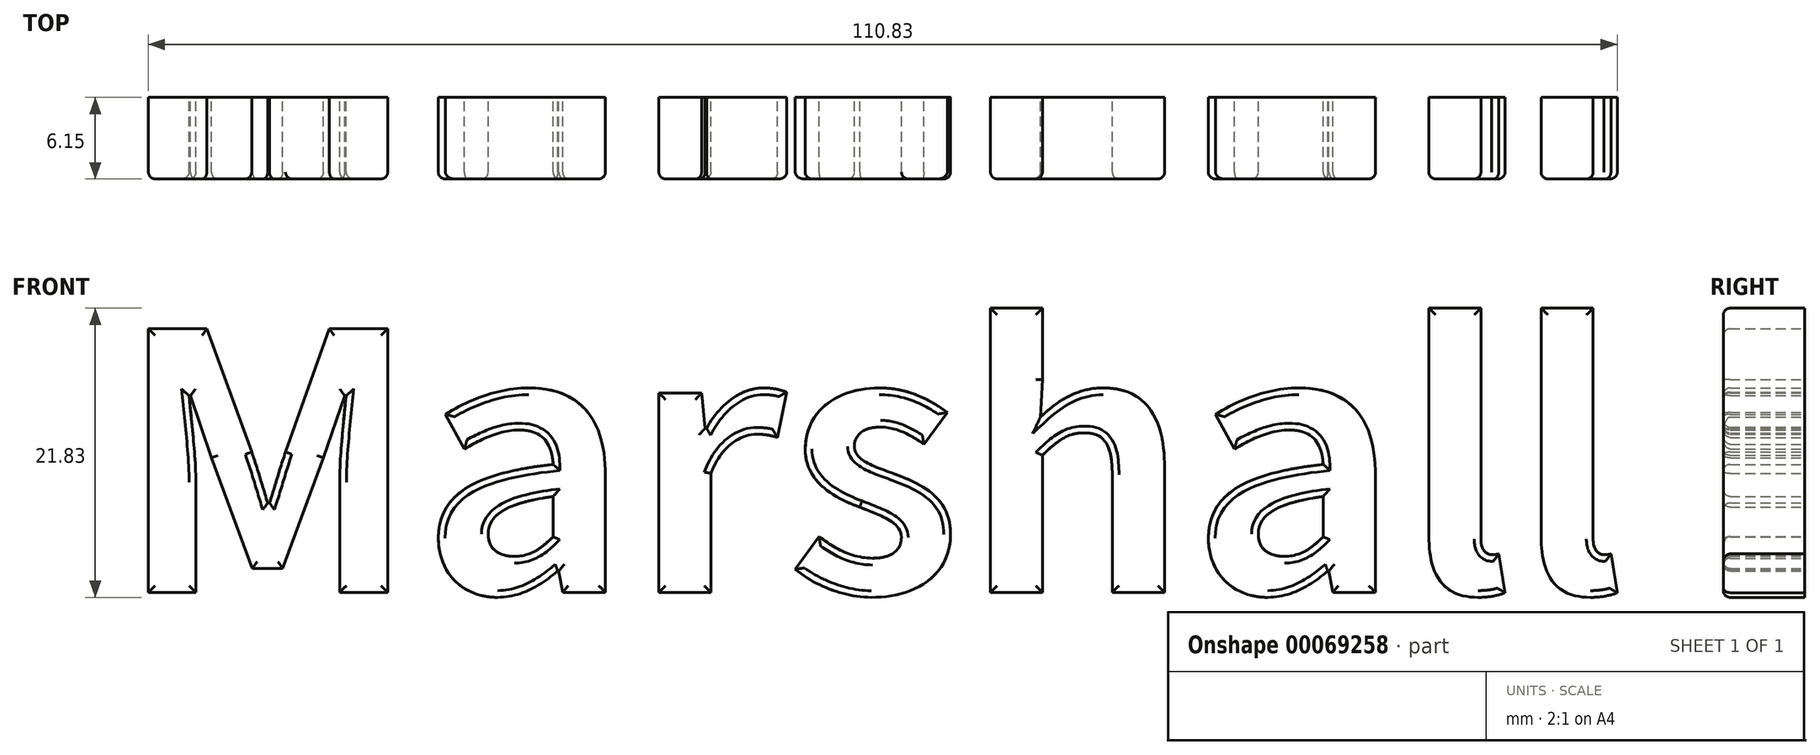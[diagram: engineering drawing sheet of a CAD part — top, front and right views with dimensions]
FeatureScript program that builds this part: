
annotation { "Feature Type Name" : "Feature", "Feature Type Description" : "" }
export const myFeature = defineFeature(function(context is Context, id is Id, definition is map)
    precondition{}
    {
        {
            var Q0;
            Q0=qCreatedBy(makeId("Front.planeOp"),FACE);
            var sketch = newSketch(context, id + "F0", { "sketchPlane" : qUnion([Q0])});
            skText(sketch, "E0", { "text": "Marshall", "fontName": "NotoSansCJKjp-Bold.otf"});
            const initialGuessF0  = {"E0": [-0.07328, 0.02694, 1, 0, 0.01935]};
            skSetInitialGuess(sketch, initialGuessF0);
            skSolve(sketch);
        }
        {
            var Q0;
            Q0 = qSketchRegion(id + "F0", true);
            extrude(context, id + "F1", {"entities" : qUnion([Q0]), "depth" : 6.15 * mm});
        }
        {
            var Q0;
            Q0=makeQuery(id+"F1.opExtrude","CAP_FACE",FACE,{"disambiguationData":[OSD([sQuery(id+"F0.wireOp",EDGE,"E0.sketch_text.stroke-0"),sQuery(id+"F0.wireOp",EDGE,"E0.sketch_text.stroke-1"),sQuery(id+"F0.wireOp",EDGE,"E0.sketch_text.stroke-2"),sQuery(id+"F0.wireOp",EDGE,"E0.sketch_text.stroke-3"),sQuery(id+"F0.wireOp",EDGE,"E0.sketch_text.stroke-4"),sQuery(id+"F0.wireOp",EDGE,"E0.sketch_text.stroke-5"),sQuery(id+"F0.wireOp",EDGE,"E0.sketch_text.stroke-6"),sQuery(id+"F0.wireOp",EDGE,"E0.sketch_text.stroke-7"),sQuery(id+"F0.wireOp",EDGE,"E0.sketch_text.stroke-8"),sQuery(id+"F0.wireOp",EDGE,"E0.sketch_text.stroke-9"),sQuery(id+"F0.wireOp",EDGE,"E0.sketch_text.stroke-10"),sQuery(id+"F0.wireOp",EDGE,"E0.sketch_text.stroke-11"),sQuery(id+"F0.wireOp",EDGE,"E0.sketch_text.stroke-12"),sQuery(id+"F0.wireOp",EDGE,"E0.sketch_text.stroke-13"),sQuery(id+"F0.wireOp",EDGE,"E0.sketch_text.stroke-14"),sQuery(id+"F0.wireOp",EDGE,"E0.sketch_text.stroke-15"),sQuery(id+"F0.wireOp",EDGE,"E0.sketch_text.stroke-16"),sQuery(id+"F0.wireOp",EDGE,"E0.sketch_text.stroke-17"),sQuery(id+"F0.wireOp",EDGE,"E0.sketch_text.stroke-18"),sQuery(id+"F0.wireOp",EDGE,"E0.sketch_text.stroke-19"),sQuery(id+"F0.wireOp",EDGE,"E0.sketch_text.stroke-20"),sQuery(id+"F0.wireOp",EDGE,"E0.sketch_text.stroke-21")])],"isStart":false});
            var Q1;
            Q1=makeQuery(id+"F1.opExtrude","CAP_FACE",FACE,{"disambiguationData":[OSD([sQuery(id+"F0.wireOp",EDGE,"E0.sketch_text.stroke-22"),sQuery(id+"F0.wireOp",EDGE,"E0.sketch_text.stroke-23"),sQuery(id+"F0.wireOp",EDGE,"E0.sketch_text.stroke-24"),sQuery(id+"F0.wireOp",EDGE,"E0.sketch_text.stroke-25"),sQuery(id+"F0.wireOp",EDGE,"E0.sketch_text.stroke-26"),sQuery(id+"F0.wireOp",EDGE,"E0.sketch_text.stroke-27"),sQuery(id+"F0.wireOp",EDGE,"E0.sketch_text.stroke-28"),sQuery(id+"F0.wireOp",EDGE,"E0.sketch_text.stroke-29"),sQuery(id+"F0.wireOp",EDGE,"E0.sketch_text.stroke-30"),sQuery(id+"F0.wireOp",EDGE,"E0.sketch_text.stroke-31"),sQuery(id+"F0.wireOp",EDGE,"E0.sketch_text.stroke-32"),sQuery(id+"F0.wireOp",EDGE,"E0.sketch_text.stroke-33"),sQuery(id+"F0.wireOp",EDGE,"E0.sketch_text.stroke-34"),sQuery(id+"F0.wireOp",EDGE,"E0.sketch_text.stroke-35"),sQuery(id+"F0.wireOp",EDGE,"E0.sketch_text.stroke-36"),sQuery(id+"F0.wireOp",EDGE,"E0.sketch_text.stroke-37")])],"isStart":false});
            var Q2;
            Q2=makeQuery(id+"F1.opExtrude","CAP_FACE",FACE,{"disambiguationData":[OSD([sQuery(id+"F0.wireOp",EDGE,"E0.sketch_text.stroke-38"),sQuery(id+"F0.wireOp",EDGE,"E0.sketch_text.stroke-39"),sQuery(id+"F0.wireOp",EDGE,"E0.sketch_text.stroke-40"),sQuery(id+"F0.wireOp",EDGE,"E0.sketch_text.stroke-41"),sQuery(id+"F0.wireOp",EDGE,"E0.sketch_text.stroke-42"),sQuery(id+"F0.wireOp",EDGE,"E0.sketch_text.stroke-43"),sQuery(id+"F0.wireOp",EDGE,"E0.sketch_text.stroke-44"),sQuery(id+"F0.wireOp",EDGE,"E0.sketch_text.stroke-45"),sQuery(id+"F0.wireOp",EDGE,"E0.sketch_text.stroke-46"),sQuery(id+"F0.wireOp",EDGE,"E0.sketch_text.stroke-47"),sQuery(id+"F0.wireOp",EDGE,"E0.sketch_text.stroke-48")])],"isStart":false});
            var Q3;
            Q3=makeQuery(id+"F1.opExtrude","CAP_FACE",FACE,{"disambiguationData":[OSD([sQuery(id+"F0.wireOp",EDGE,"E0.sketch_text.stroke-49"),sQuery(id+"F0.wireOp",EDGE,"E0.sketch_text.stroke-50"),sQuery(id+"F0.wireOp",EDGE,"E0.sketch_text.stroke-51"),sQuery(id+"F0.wireOp",EDGE,"E0.sketch_text.stroke-52"),sQuery(id+"F0.wireOp",EDGE,"E0.sketch_text.stroke-53"),sQuery(id+"F0.wireOp",EDGE,"E0.sketch_text.stroke-54"),sQuery(id+"F0.wireOp",EDGE,"E0.sketch_text.stroke-55"),sQuery(id+"F0.wireOp",EDGE,"E0.sketch_text.stroke-56"),sQuery(id+"F0.wireOp",EDGE,"E0.sketch_text.stroke-57"),sQuery(id+"F0.wireOp",EDGE,"E0.sketch_text.stroke-58"),sQuery(id+"F0.wireOp",EDGE,"E0.sketch_text.stroke-59"),sQuery(id+"F0.wireOp",EDGE,"E0.sketch_text.stroke-60"),sQuery(id+"F0.wireOp",EDGE,"E0.sketch_text.stroke-61"),sQuery(id+"F0.wireOp",EDGE,"E0.sketch_text.stroke-62")])],"isStart":false});
            var Q4;
            Q4=makeQuery(id+"F1.opExtrude","CAP_FACE",FACE,{"disambiguationData":[OSD([sQuery(id+"F0.wireOp",EDGE,"E0.sketch_text.stroke-63"),sQuery(id+"F0.wireOp",EDGE,"E0.sketch_text.stroke-64"),sQuery(id+"F0.wireOp",EDGE,"E0.sketch_text.stroke-65"),sQuery(id+"F0.wireOp",EDGE,"E0.sketch_text.stroke-66"),sQuery(id+"F0.wireOp",EDGE,"E0.sketch_text.stroke-67"),sQuery(id+"F0.wireOp",EDGE,"E0.sketch_text.stroke-68"),sQuery(id+"F0.wireOp",EDGE,"E0.sketch_text.stroke-69"),sQuery(id+"F0.wireOp",EDGE,"E0.sketch_text.stroke-70"),sQuery(id+"F0.wireOp",EDGE,"E0.sketch_text.stroke-71"),sQuery(id+"F0.wireOp",EDGE,"E0.sketch_text.stroke-72"),sQuery(id+"F0.wireOp",EDGE,"E0.sketch_text.stroke-73"),sQuery(id+"F0.wireOp",EDGE,"E0.sketch_text.stroke-74"),sQuery(id+"F0.wireOp",EDGE,"E0.sketch_text.stroke-75")])],"isStart":false});
            var Q5;
            Q5=makeQuery(id+"F1.opExtrude","CAP_FACE",FACE,{"disambiguationData":[OSD([sQuery(id+"F0.wireOp",EDGE,"E0.sketch_text.stroke-76"),sQuery(id+"F0.wireOp",EDGE,"E0.sketch_text.stroke-77"),sQuery(id+"F0.wireOp",EDGE,"E0.sketch_text.stroke-78"),sQuery(id+"F0.wireOp",EDGE,"E0.sketch_text.stroke-79"),sQuery(id+"F0.wireOp",EDGE,"E0.sketch_text.stroke-80"),sQuery(id+"F0.wireOp",EDGE,"E0.sketch_text.stroke-81"),sQuery(id+"F0.wireOp",EDGE,"E0.sketch_text.stroke-82"),sQuery(id+"F0.wireOp",EDGE,"E0.sketch_text.stroke-83"),sQuery(id+"F0.wireOp",EDGE,"E0.sketch_text.stroke-84"),sQuery(id+"F0.wireOp",EDGE,"E0.sketch_text.stroke-85"),sQuery(id+"F0.wireOp",EDGE,"E0.sketch_text.stroke-86"),sQuery(id+"F0.wireOp",EDGE,"E0.sketch_text.stroke-87"),sQuery(id+"F0.wireOp",EDGE,"E0.sketch_text.stroke-88"),sQuery(id+"F0.wireOp",EDGE,"E0.sketch_text.stroke-89"),sQuery(id+"F0.wireOp",EDGE,"E0.sketch_text.stroke-90"),sQuery(id+"F0.wireOp",EDGE,"E0.sketch_text.stroke-91")])],"isStart":false});
            var Q6;
            Q6=makeQuery(id+"F1.opExtrude","CAP_FACE",FACE,{"disambiguationData":[OSD([sQuery(id+"F0.wireOp",EDGE,"E0.sketch_text.stroke-92"),sQuery(id+"F0.wireOp",EDGE,"E0.sketch_text.stroke-93"),sQuery(id+"F0.wireOp",EDGE,"E0.sketch_text.stroke-94"),sQuery(id+"F0.wireOp",EDGE,"E0.sketch_text.stroke-95"),sQuery(id+"F0.wireOp",EDGE,"E0.sketch_text.stroke-96"),sQuery(id+"F0.wireOp",EDGE,"E0.sketch_text.stroke-97"),sQuery(id+"F0.wireOp",EDGE,"E0.sketch_text.stroke-98"),sQuery(id+"F0.wireOp",EDGE,"E0.sketch_text.stroke-99")])],"isStart":false});
            var Q7;
            Q7=makeQuery(id+"F1.opExtrude","CAP_FACE",FACE,{"disambiguationData":[OSD([sQuery(id+"F0.wireOp",EDGE,"E0.sketch_text.stroke-100"),sQuery(id+"F0.wireOp",EDGE,"E0.sketch_text.stroke-101"),sQuery(id+"F0.wireOp",EDGE,"E0.sketch_text.stroke-102"),sQuery(id+"F0.wireOp",EDGE,"E0.sketch_text.stroke-103"),sQuery(id+"F0.wireOp",EDGE,"E0.sketch_text.stroke-104"),sQuery(id+"F0.wireOp",EDGE,"E0.sketch_text.stroke-105"),sQuery(id+"F0.wireOp",EDGE,"E0.sketch_text.stroke-106"),sQuery(id+"F0.wireOp",EDGE,"E0.sketch_text.stroke-107")])],"isStart":false});
            fillet(context, id + "F2", {"entities" : qUnion([Q0, Q1, Q2, Q3, Q4, Q5, Q6, Q7]), "radius" : 0.5 * mm, "tangentPropagation" : true, "allowEdgeOverflow" : false});
        }
    });
